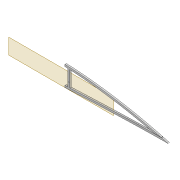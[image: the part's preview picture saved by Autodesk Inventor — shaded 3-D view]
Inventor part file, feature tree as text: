
AUTODESK INVENTOR PART (.ipt)
format: ipt  version: 2022 (Build 260153000, 153)  size: 411,136 bytes
history: native  units: mm
features: extrude x8, sketch x7, projected_geometry x6, fillet x2, shell x1, plane x1
ambient origin geometry x8: Origin, YZ Plane, XZ Plane, XY Plane, X Axis, Y Axis, Z Axis, Center Point
bodies: Solid1 (feature_tree)
feature tree (25):
  extrude  "Extrusion1"  Depth=5.0mm
  shell  "Shell1"  Thickness=2.0mm
  extrude  "Extrusion8"  Depth=5.9mm
  extrude  "Extrusion3"  Depth=10.0mm TaperAngle=0.0deg
  extrude  "Extrusion4"  Depth=2.0mm
  fillet  "Fillet1"  Radius=5.0mm
  sketch  "Sketch10"  dims[d22=4.0mm d23=0.0mm d31=2.0mm d32=5.0mm]
  extrude  "Extrusion5"  Depth=2.5mm
  plane  "Work Plane2"
  extrude  "Extrusion9"  Depth=1.6mm
  fillet  "Fillet2"  Radius=2.5mm
  extrude  "Extrusion10"  Depth=6.0mm
  extrude  "Extrusion11"  Depth=4.0mm TaperAngle=0.0deg
  sketch  "Sketch3"  dims[d0=4.0mm d1=0.0mm d2=5.0mm d7=2.0mm]
  sketch  "Sketch8"  dims[d8=2.0mm d9=5.9mm]
  sketch  "Sketch9"  dims[d13=10.0mm d14=0.0mm d16=10.0mm d17=0.0mm]
  projected_geometry  "Projected Loop4"
  projected_geometry  "Projected Loop10"
  sketch  "Sketch24"  dims[d34=1.6mm d35=2.5mm]
  projected_geometry  "Projected Loop11"
  projected_geometry  "Projected Loop12"
  projected_geometry  "Projected Loop13"
  sketch  "Sketch26"  dims[d37=5.0mm d38=1.6mm d40=2.5mm]
  projected_geometry  "Projected Loop14"
  sketch  "Sketch27"  dims[d62=80.0mm d63=6.0mm d64=4.0mm d65=0.0mm d66=3.0mm d67=12.0mm d68=5.0mm d69=15.0mm d70=12.0mm d71=3.05mm d72=10.0mm d73=0.0mm d74=2.0mm d75=90.0mm d76=20.0mm d77=0.5mm d78=10.0mm d79=0.0mm d80=10.0mm d81=0.0mm]
